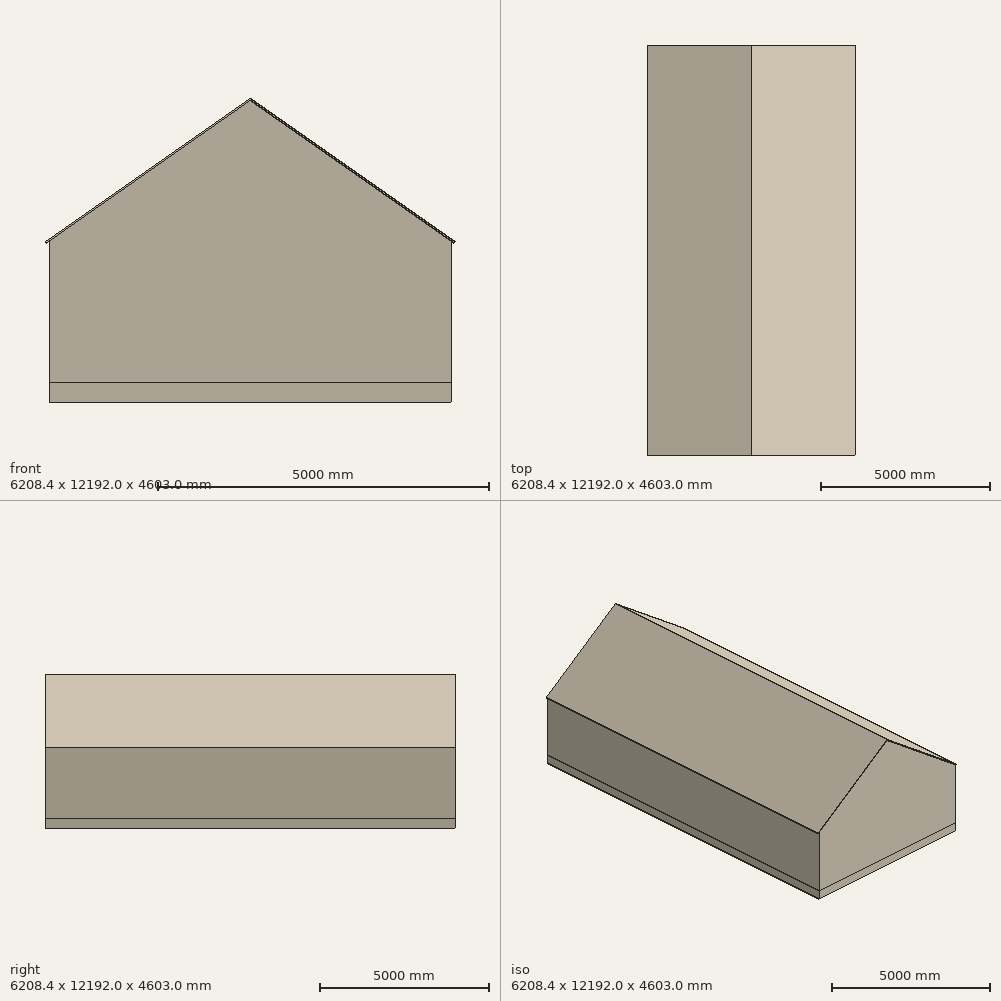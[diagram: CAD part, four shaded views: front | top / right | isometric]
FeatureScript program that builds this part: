
annotation { "Feature Type Name" : "Feature", "Feature Type Description" : "" }
export const myFeature = defineFeature(function(context is Context, id is Id, definition is map)
    precondition{}
    {
        {
            var Q0;
            Q0=qCreatedBy(makeId("Top.planeOp"),FACE);
            var sketch = newSketch(context, id + "F0", { "sketchPlane" : qUnion([Q0])});
            skLineSegment(sketch, "E0.bottom", {"start": v(3048, 6096) * mm, "end": v(-3048, 6096) * mm});
            skLineSegment(sketch, "E0.top", {"start": v(3048, -6096) * mm, "end": v(-3048, -6096) * mm});
            skLineSegment(sketch, "E0.left", {"start": v(3048, 6096) * mm, "end": v(3048, -6096) * mm});
            skLineSegment(sketch, "E0.right", {"start": v(-3048, 6096) * mm, "end": v(-3048, -6096) * mm});
            skPoint(sketch, "E0.middle", {"position": v(0, 0) * mm});
            skSolve(sketch);
        }
        {
            var Q0;
            Q0=makeQuery(id+"F0.imprint","IMPRINT",FACE,{"disambiguationData":[TD([[makeQuery(id+"F0.imprint","IMPRINT",EDGE,{"derivedFrom":sQuery(id+"F0.wireOp",EDGE,"E0.bottom")}),1.0]])]});
            extrude(context, id + "F1", {"entities" : qUnion([Q0]), "oppositeDirection" : true, "depth" : 304.8 * mm});
        }
        {
            var Q0;
            Q0=qCreatedBy(makeId("Top.planeOp"),FACE);
            var sketch = newSketch(context, id + "F2", { "sketchPlane" : qUnion([Q0])});
            skLineSegment(sketch, "E1.0.0", {"start": v(-3048, -6096) * mm, "end": v(3048, -6096) * mm});
            skLineSegment(sketch, "E1.0.1", {"start": v(3048, -6096) * mm, "end": v(3048, 6096) * mm});
            skLineSegment(sketch, "E1.0.2", {"start": v(3048, 6096) * mm, "end": v(-3048, 6096) * mm});
            skLineSegment(sketch, "E1.0.3", {"start": v(-3048, 6096) * mm, "end": v(-3048, -6096) * mm});
            skLineSegment(sketch, "E2.bottom", {"start": v(2895.6, 5943.6) * mm, "end": v(-2895.6, 5943.6) * mm});
            skLineSegment(sketch, "E2.top", {"start": v(2895.6, -5943.6) * mm, "end": v(-2895.6, -5943.6) * mm});
            skLineSegment(sketch, "E2.left", {"start": v(2895.6, 5943.6) * mm, "end": v(2895.6, -5943.6) * mm});
            skLineSegment(sketch, "E2.right", {"start": v(-2895.6, 5943.6) * mm, "end": v(-2895.6, -5943.6) * mm});
            skPoint(sketch, "E2.middle", {"position": v(0, 0) * mm});
            skSolve(sketch);
        }
        {
            var Q0;
            Q0=makeQuery(id+"F2.imprint","IMPRINT",FACE,{"disambiguationData":[TD([[makeQuery(id+"F2.imprint","IMPRINT",EDGE,{"derivedFrom":sQuery(id+"F2.wireOp",EDGE,"E1.0.0")}),1.0]])]});
            extrude(context, id + "F3", {"entities" : qUnion([Q0]), "depth" : 2133.6 * mm});
        }
        {
            var Q0;
            Q0=makeQuery(id+"F3.opExtrude","SWEPT_FACE",FACE,{"disambiguationData":[OSD([sQuery(id+"F2.wireOp",EDGE,"E1.0.0")])]});
            var sketch = newSketch(context, id + "F4", { "sketchPlane" : qUnion([Q0])});
            skLineSegment(sketch, "E3.0", {"start": v(-3048, 2133.6) * mm, "end": v(3048, 2133.6) * mm});
            skLineSegment(sketch, "E4", {"start": v(-3048, 2133.6) * mm, "end": v(0, 4267.2) * mm});
            skLineSegment(sketch, "E5", {"start": v(0, 4267.2) * mm, "end": v(3048, 2133.6) * mm});
            skSolve(sketch);
        }
        {
            var Q0;
            Q0=makeQuery(id+"F4.imprint","IMPRINT",FACE,{"disambiguationData":[TD([[makeQuery(id+"F4.imprint","IMPRINT",EDGE,{"derivedFrom":sQuery(id+"F4.wireOp",EDGE,"E3.0")}),1.0]])]});
            extrude(context, id + "F5", {"entities" : qUnion([Q0]), "operationType" : NewBodyOperationType.ADD, "oppositeDirection" : true, "depth" : 152.4 * mm});
        }
        {
            var Q0;
            Q0=makeQuery(id+"F3.opExtrude","SWEPT_FACE",FACE,{"disambiguationData":[OSD([sQuery(id+"F2.wireOp",EDGE,"E1.0.2")])]});
            var sketch = newSketch(context, id + "F6", { "sketchPlane" : qUnion([Q0])});
            skLineSegment(sketch, "E6.0", {"start": v(-3048, 2133.6) * mm, "end": v(3048, 2133.6) * mm});
            skLineSegment(sketch, "E7.0", {"start": v(0, 4267.2) * mm, "end": v(-3048, 2133.6) * mm});
            skLineSegment(sketch, "E8.0", {"start": v(3048, 2133.6) * mm, "end": v(0, 4267.2) * mm});
            skSolve(sketch);
        }
        {
            var Q0;
            Q0=makeQuery(id+"F6.imprint","IMPRINT",FACE,{"disambiguationData":[TD([[makeQuery(id+"F6.imprint","IMPRINT",EDGE,{"derivedFrom":sQuery(id+"F6.wireOp",EDGE,"E6.0")}),1.0]])]});
            extrude(context, id + "F7", {"entities" : qUnion([Q0]), "operationType" : NewBodyOperationType.ADD, "oppositeDirection" : true, "depth" : 152.4 * mm});
        }
        {
            var Q0;
            Q0=makeQuery(id+"F5.boolean.opBoolean","MERGE",FACE,{"derivedFrom":[makeQuery(id+"F3.opExtrude","SWEPT_FACE",FACE,{"disambiguationData":[OSD([sQuery(id+"F2.wireOp",EDGE,"E1.0.0")])]}),makeQuery(id+"F5.opExtrude","CAP_FACE",FACE,{"disambiguationData":[OSD([sQuery(id+"F4.wireOp",EDGE,"E3.0"),sQuery(id+"F4.wireOp",EDGE,"E4"),sQuery(id+"F4.wireOp",EDGE,"E5")])],"isStart":true})]});
            var sketch = newSketch(context, id + "F8", { "sketchPlane" : qUnion([Q0])});
            skLineSegment(sketch, "E9.0", {"start": v(-3048, 2133.6) * mm, "end": v(0, 4267.2) * mm});
            skLineSegment(sketch, "E10.0", {"start": v(0, 4267.2) * mm, "end": v(3048, 2133.6) * mm});
            skLineSegment(sketch, "E11", {"start": v(-3048, 2133.6) * mm, "end": v(-3089.62, 2104.47) * mm});
            skLineSegment(sketch, "E12", {"start": v(-3089.62, 2104.47) * mm, "end": v(-3104.18, 2125.28) * mm});
            skLineSegment(sketch, "E13", {"start": v(-3104.18, 2125.28) * mm, "end": v(0, 4298.2) * mm});
            skLineSegment(sketch, "E14", {"start": v(0, 4298.2) * mm, "end": v(3104.18, 2125.28) * mm});
            skLineSegment(sketch, "E15", {"start": v(3104.18, 2125.28) * mm, "end": v(3089.62, 2104.47) * mm});
            skLineSegment(sketch, "E16", {"start": v(3089.62, 2104.47) * mm, "end": v(3048, 2133.6) * mm});
            skSolve(sketch);
        }
        {
            var Q0;
            Q0=makeQuery(id+"F8.imprint","IMPRINT",FACE,{"disambiguationData":[TD([[makeQuery(id+"F8.imprint","IMPRINT",EDGE,{"derivedFrom":sQuery(id+"F8.wireOp",EDGE,"E9.0")}),1.0]])]});
            var Q1;
            Q1=makeQuery(id+"F7.boolean.opBoolean","MERGE",FACE,{"derivedFrom":[makeQuery(id+"F3.opExtrude","SWEPT_FACE",FACE,{"disambiguationData":[OSD([sQuery(id+"F2.wireOp",EDGE,"E1.0.2")])]}),makeQuery(id+"F7.opExtrude","CAP_FACE",FACE,{"disambiguationData":[OSD([sQuery(id+"F6.wireOp",EDGE,"E6.0"),sQuery(id+"F6.wireOp",EDGE,"E7.0"),sQuery(id+"F6.wireOp",EDGE,"E8.0")])],"isStart":true})]});
            extrude(context, id + "F9", {"entities" : qUnion([Q0]), "endBound" : BoundingType.UP_TO_SURFACE, "oppositeDirection" : true, "endBoundEntityFace" : qUnion([Q1]), "depth" : 25.4 * mm});
        }
    });
